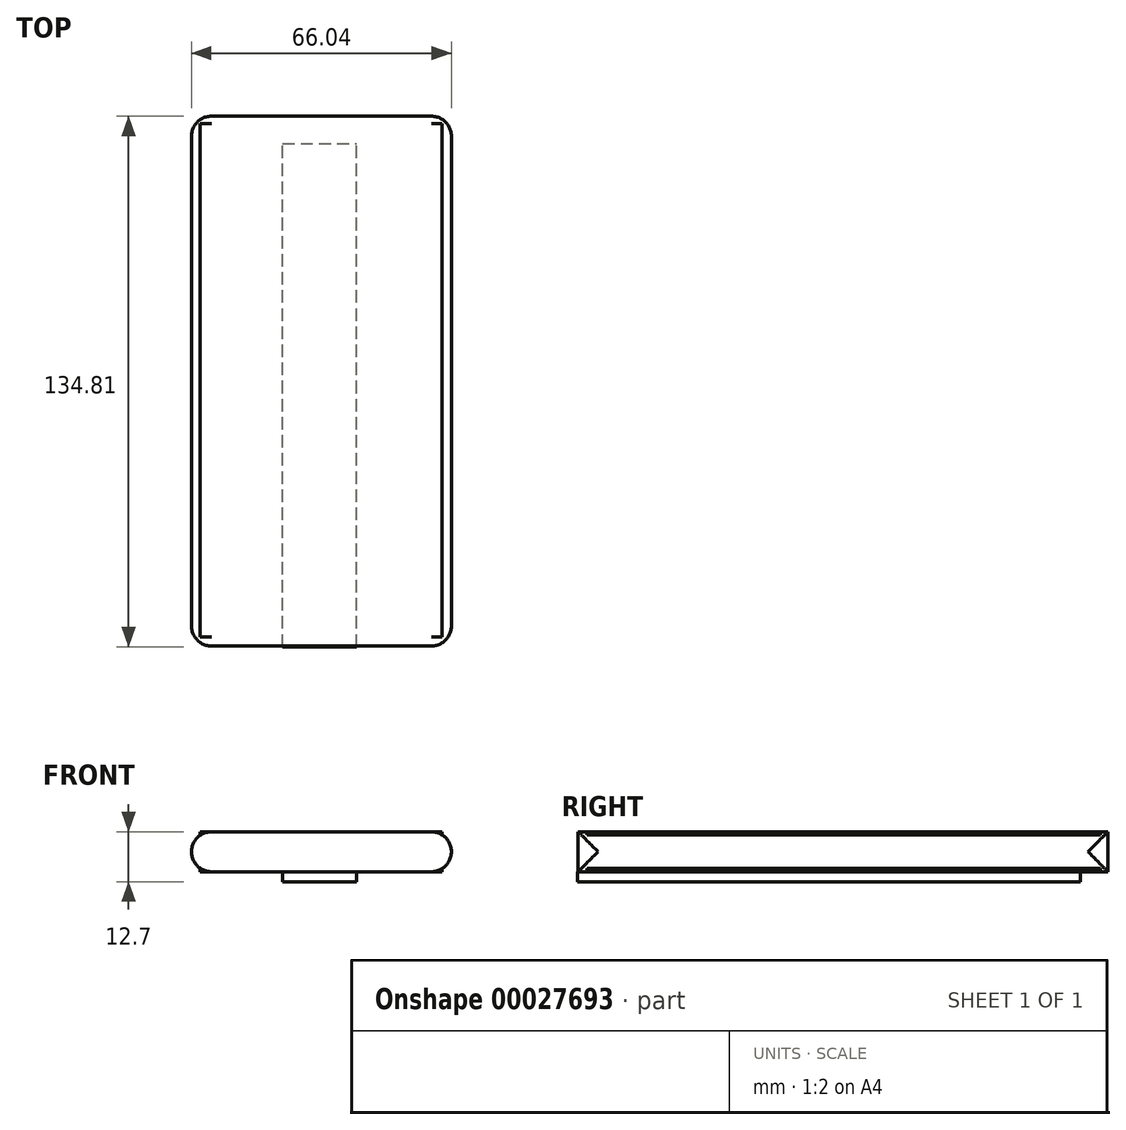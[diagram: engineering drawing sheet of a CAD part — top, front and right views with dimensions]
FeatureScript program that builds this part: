
annotation { "Feature Type Name" : "Feature", "Feature Type Description" : "" }
export const myFeature = defineFeature(function(context is Context, id is Id, definition is map)
    precondition{}
    {
        {
            var Q0;
            Q0=qCreatedBy(makeId("Top.planeOp"),FACE);
            var sketch = newSketch(context, id + "F0", { "sketchPlane" : qUnion([Q0])});
            skLineSegment(sketch, "E0.bottom", {"start": v(-36.64, 82.12) * mm, "end": v(29.4, 82.12) * mm});
            skLineSegment(sketch, "E0.top", {"start": v(-36.64, -52.5) * mm, "end": v(29.4, -52.5) * mm});
            skLineSegment(sketch, "E0.left", {"start": v(-36.64, 82.12) * mm, "end": v(-36.64, -52.5) * mm});
            skLineSegment(sketch, "E0.right", {"start": v(29.4, 82.12) * mm, "end": v(29.4, -52.5) * mm});
            skSolve(sketch);
        }
        {
            var Q0;
            Q0=makeQuery(id+"F0.imprint","IMPRINT",FACE,{"disambiguationData":[TD([[makeQuery(id+"F0.imprint","IMPRINT",EDGE,{"derivedFrom":sQuery(id+"F0.wireOp",EDGE,"E0.bottom")}),-1.0]])]});
            extrude(context, id + "F1", {"entities" : qUnion([Q0]), "depth" : 10.16 * mm});
        }
        {
            var Q0;
            Q0=makeQuery(id+"F1.opExtrude","CAP_FACE",FACE,{"disambiguationData":[OSD([sQuery(id+"F0.wireOp",EDGE,"E0.bottom"),sQuery(id+"F0.wireOp",EDGE,"E0.top"),sQuery(id+"F0.wireOp",EDGE,"E0.left"),sQuery(id+"F0.wireOp",EDGE,"E0.right")])],"isStart":false});
            shell(context, id + "F2", {"entities" : qUnion([Q0]), "thickness" : 2.54 * mm});
        }
        {
            var Q0;
            Q0=makeQuery(id+"F1.opExtrude","SWEPT_FACE",FACE,{"disambiguationData":[OSD([sQuery(id+"F0.wireOp",EDGE,"E0.left")])]});
            var Q1;
            Q1=makeQuery(id+"F1.opExtrude","SWEPT_FACE",FACE,{"disambiguationData":[OSD([sQuery(id+"F0.wireOp",EDGE,"E0.right")])]});
            var Q2;
            Q2=makeQuery(id+"F2.opShell","OFFSET_FACE",FACE,{"disambiguationData":[OSD([sQuery(id+"F0.wireOp",EDGE,"E0.bottom"),sQuery(id+"F0.wireOp",EDGE,"E0.top"),sQuery(id+"F0.wireOp",EDGE,"E0.left"),sQuery(id+"F0.wireOp",EDGE,"E0.right")])]});
            fillet(context, id + "F3", {"entities" : qUnion([Q0, Q1, Q2]), "radius" : 5.08 * mm, "tangentPropagation" : true, "allowEdgeOverflow" : false});
        }
        {
            var Q0;
            Q0=qCreatedBy(makeId("Top.planeOp"),FACE);
            var sketch = newSketch(context, id + "F4", { "sketchPlane" : qUnion([Q0])});
            skLineSegment(sketch, "E1.bottom", {"start": v(-34.39, 80.18) * mm, "end": v(27.06, 80.18) * mm});
            skLineSegment(sketch, "E1.top", {"start": v(-34.39, -50.25) * mm, "end": v(27.06, -50.25) * mm});
            skLineSegment(sketch, "E1.left", {"start": v(-34.39, 80.18) * mm, "end": v(-34.39, -50.25) * mm});
            skLineSegment(sketch, "E1.right", {"start": v(27.06, 80.18) * mm, "end": v(27.06, -50.25) * mm});
            skSolve(sketch);
        }
        {
            var Q0;
            Q0 = qSketchRegion(id + "F4", true);
            extrude(context, id + "F5", {"entities" : qUnion([Q0]), "operationType" : NewBodyOperationType.ADD, "depth" : 10.16 * mm});
        }
        {
            var Q0;
            Q0=qCreatedBy(makeId("Top.planeOp"),FACE);
            var sketch = newSketch(context, id + "F6", { "sketchPlane" : qUnion([Q0])});
            skLineSegment(sketch, "E2.bottom", {"start": v(-13.43, -52.69) * mm, "end": v(5.3, -52.69) * mm});
            skLineSegment(sketch, "E2.top", {"start": v(-13.43, 75.1) * mm, "end": v(5.3, 75.1) * mm});
            skLineSegment(sketch, "E2.left", {"start": v(-13.43, -52.69) * mm, "end": v(-13.43, 75.1) * mm});
            skLineSegment(sketch, "E2.right", {"start": v(5.3, -52.69) * mm, "end": v(5.3, 75.1) * mm});
            skSolve(sketch);
        }
        {
            var Q0;
            Q0 = qSketchRegion(id + "F6", true);
            extrude(context, id + "F7", {"entities" : qUnion([Q0]), "operationType" : NewBodyOperationType.ADD, "oppositeDirection" : true, "depth" : 2.54 * mm});
        }
    });
